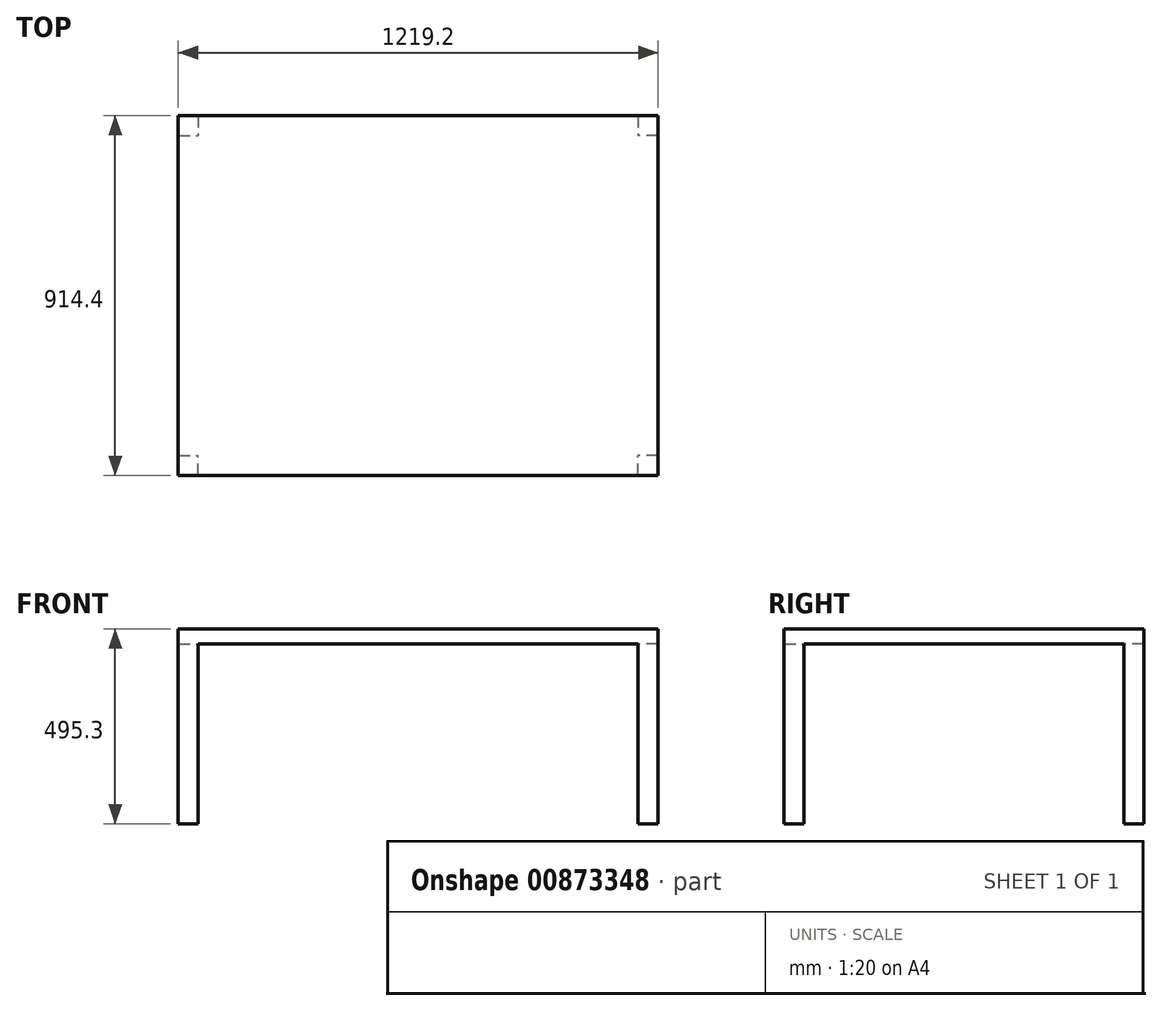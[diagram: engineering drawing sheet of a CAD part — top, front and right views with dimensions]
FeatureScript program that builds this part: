
annotation { "Feature Type Name" : "Feature", "Feature Type Description" : "" }
export const myFeature = defineFeature(function(context is Context, id is Id, definition is map)
    precondition{}
    {
        {
            var Q0;
            Q0=qCreatedBy(makeId("Top.planeOp"),FACE);
            var sketch = newSketch(context, id + "F0", { "sketchPlane" : qUnion([Q0])});
            skLineSegment(sketch, "E0.bottom", {"start": v(-609.6, -457.2) * mm, "end": v(609.6, -457.2) * mm});
            skLineSegment(sketch, "E0.top", {"start": v(-609.6, 457.2) * mm, "end": v(609.6, 457.2) * mm});
            skLineSegment(sketch, "E0.left", {"start": v(-609.6, -457.2) * mm, "end": v(-609.6, 457.2) * mm});
            skLineSegment(sketch, "E0.right", {"start": v(609.6, -457.2) * mm, "end": v(609.6, 457.2) * mm});
            skPoint(sketch, "E0.middle", {"position": v(0, 0) * mm});
            skSolve(sketch);
        }
        {
            var Q0;
            Q0=makeQuery(id+"F0.imprint","IMPRINT",FACE,{"disambiguationData":[TD([[makeQuery(id+"F0.imprint","IMPRINT",EDGE,{"derivedFrom":sQuery(id+"F0.wireOp",EDGE,"E0.bottom")}),1.0]])]});
            extrude(context, id + "F1", {"entities" : qUnion([Q0]), "endBound" : BoundingType.SYMMETRIC, "depth" : 38.1 * mm, "offsetDistance" : 25.4 * mm});
        }
        {
            var Q0;
            Q0=makeQuery(id+"F1.opExtrude","CAP_FACE",FACE,{"disambiguationData":[OSD([sQuery(id+"F0.wireOp",EDGE,"E0.bottom"),sQuery(id+"F0.wireOp",EDGE,"E0.top"),sQuery(id+"F0.wireOp",EDGE,"E0.left"),sQuery(id+"F0.wireOp",EDGE,"E0.right")])],"isStart":true});
            var sketch = newSketch(context, id + "F2", { "sketchPlane" : qUnion([Q0])});
            skLineSegment(sketch, "E1.bottom", {"start": v(609.6, 457.2) * mm, "end": v(558.8, 457.2) * mm});
            skLineSegment(sketch, "E1.top", {"start": v(609.6, 406.4) * mm, "end": v(558.8, 406.4) * mm});
            skLineSegment(sketch, "E1.left", {"start": v(609.6, 457.2) * mm, "end": v(609.6, 406.4) * mm});
            skLineSegment(sketch, "E1.right", {"start": v(558.8, 457.2) * mm, "end": v(558.8, 406.4) * mm});
            skLineSegment(sketch, "E2.bottom", {"start": v(609.6, -457.2) * mm, "end": v(558.8, -457.2) * mm});
            skLineSegment(sketch, "E2.top", {"start": v(609.6, -406.4) * mm, "end": v(558.8, -406.4) * mm});
            skLineSegment(sketch, "E2.left", {"start": v(609.6, -457.2) * mm, "end": v(609.6, -406.4) * mm});
            skLineSegment(sketch, "E2.right", {"start": v(558.8, -457.2) * mm, "end": v(558.8, -406.4) * mm});
            skLineSegment(sketch, "E3.bottom", {"start": v(-609.6, -457.2) * mm, "end": v(-558.8, -457.2) * mm});
            skLineSegment(sketch, "E3.top", {"start": v(-609.6, -406.4) * mm, "end": v(-558.8, -406.4) * mm});
            skLineSegment(sketch, "E3.left", {"start": v(-609.6, -457.2) * mm, "end": v(-609.6, -406.4) * mm});
            skLineSegment(sketch, "E3.right", {"start": v(-558.8, -457.2) * mm, "end": v(-558.8, -406.4) * mm});
            skLineSegment(sketch, "E4.bottom", {"start": v(-609.6, 457.2) * mm, "end": v(-558.8, 457.2) * mm});
            skLineSegment(sketch, "E4.top", {"start": v(-609.6, 406.4) * mm, "end": v(-558.8, 406.4) * mm});
            skLineSegment(sketch, "E4.left", {"start": v(-609.6, 457.2) * mm, "end": v(-609.6, 406.4) * mm});
            skLineSegment(sketch, "E4.right", {"start": v(-558.8, 457.2) * mm, "end": v(-558.8, 406.4) * mm});
            skSolve(sketch);
        }
        {
            var Q0;
            Q0 = qSketchRegion(id + "F2", true);
            extrude(context, id + "F3", {"entities" : qUnion([Q0]), "operationType" : NewBodyOperationType.ADD, "depth" : 457.2 * mm, "offsetDistance" : 25.4 * mm});
        }
    });
